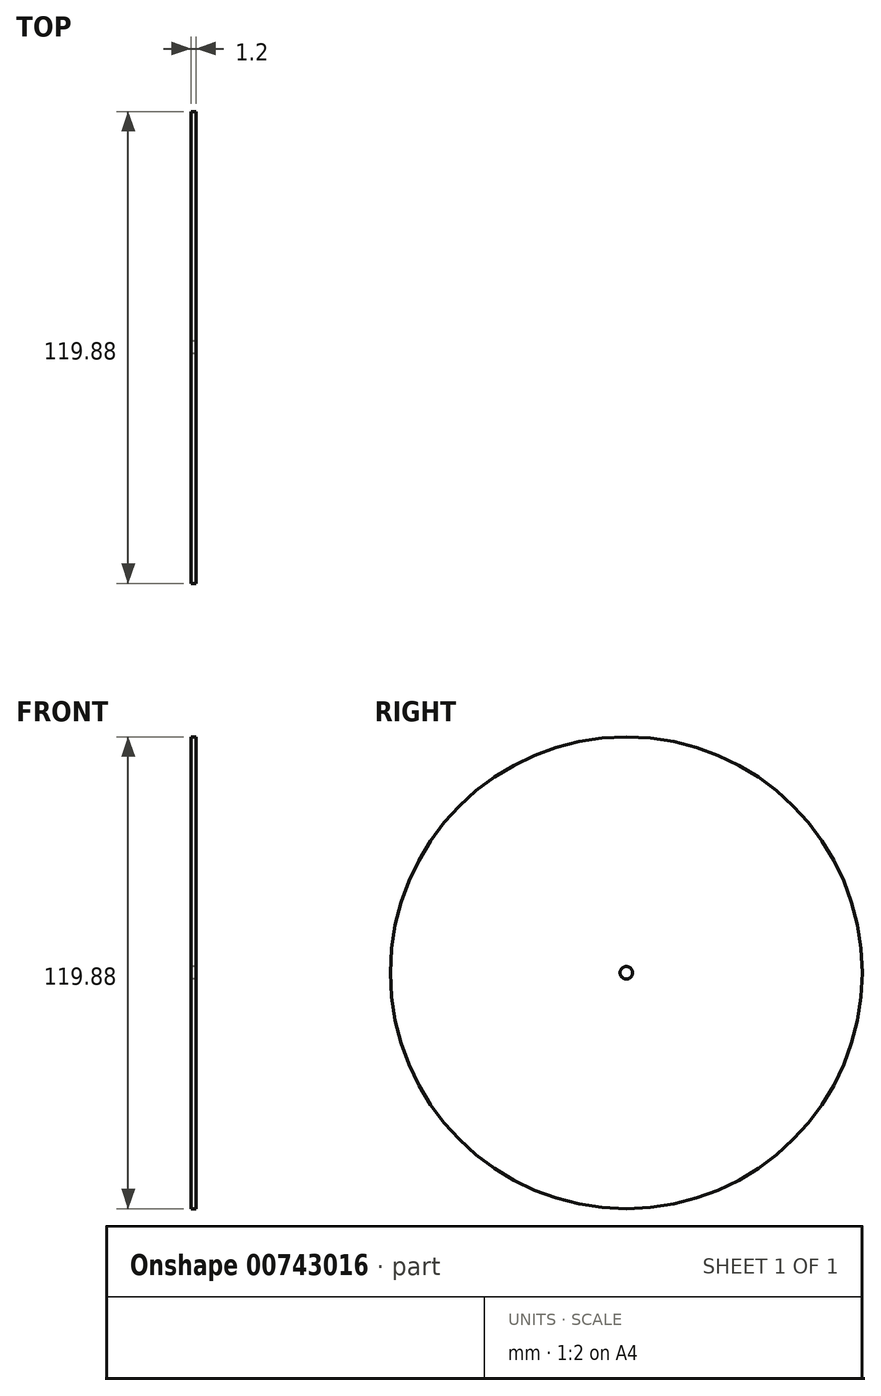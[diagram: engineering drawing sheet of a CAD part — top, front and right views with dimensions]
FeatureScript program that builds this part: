
annotation { "Feature Type Name" : "Feature", "Feature Type Description" : "" }
export const myFeature = defineFeature(function(context is Context, id is Id, definition is map)
    precondition{}
    {
        {
            var Q0;
            Q0=qCreatedBy(makeId("Right.planeOp"),FACE);
            var sketch = newSketch(context, id + "F0", { "sketchPlane" : qUnion([Q0])});
            skCircle(sketch, "E0", {"center": v(0, 0) * mm, "radius": 59.94 * mm});
            skCircle(sketch, "E1", {"center": v(0, 0) * mm, "radius": 1.59 * mm});
            skSolve(sketch);
        }
        {
            var Q0;
            Q0=makeQuery(id+"F0.imprint","IMPRINT",FACE,{"disambiguationData":[TD([[makeQuery(id+"F0.imprint","IMPRINT",EDGE,{"derivedFrom":sQuery(id+"F0.wireOp",EDGE,"E0")}),1.0]])]});
            extrude(context, id + "F1", {"entities" : qUnion([Q0]), "depth" : 1.2 * mm, "offsetDistance" : 25.4 * mm});
        }
    });
